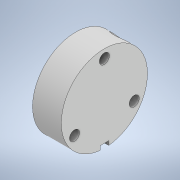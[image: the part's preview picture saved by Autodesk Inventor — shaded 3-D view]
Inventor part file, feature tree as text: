
AUTODESK INVENTOR PART (.ipt)
format: ipt  version: 2022 (Build 260153000, 153)  size: 163,328 bytes
history: native  units: mm
features: sketch x5, other x2, revolve x2, hole x2, extrude x1
ambient origin geometry x8: Origin, YZ Plane, XZ Plane, XY Plane, X Axis, Y Axis, Z Axis, Center Point
bodies: Body1 (feature_tree)
feature tree (12):
  other  "Твердое тело1"
  revolve  "Вращение1"
  hole  "Отверстие1"  [1 undecoded]
  hole  "Отверстие2"  [1 undecoded]
  extrude  "Выдавливание1"  TaperAngle=90.0deg  [1 undecoded]
  other  "РабПлоскость1"
  revolve  "Вращение3"
  sketch  "Эскиз1"
  sketch  "Эскиз2"
  sketch  "Эскиз3"
  sketch  "Эскиз4"
  sketch  "Эскиз5"
note: 3 required parameter values undecoded (feature->parameter linkage not recoverable at this tier; creation-order binding heuristic only, values carry confidence <= 0.55)
